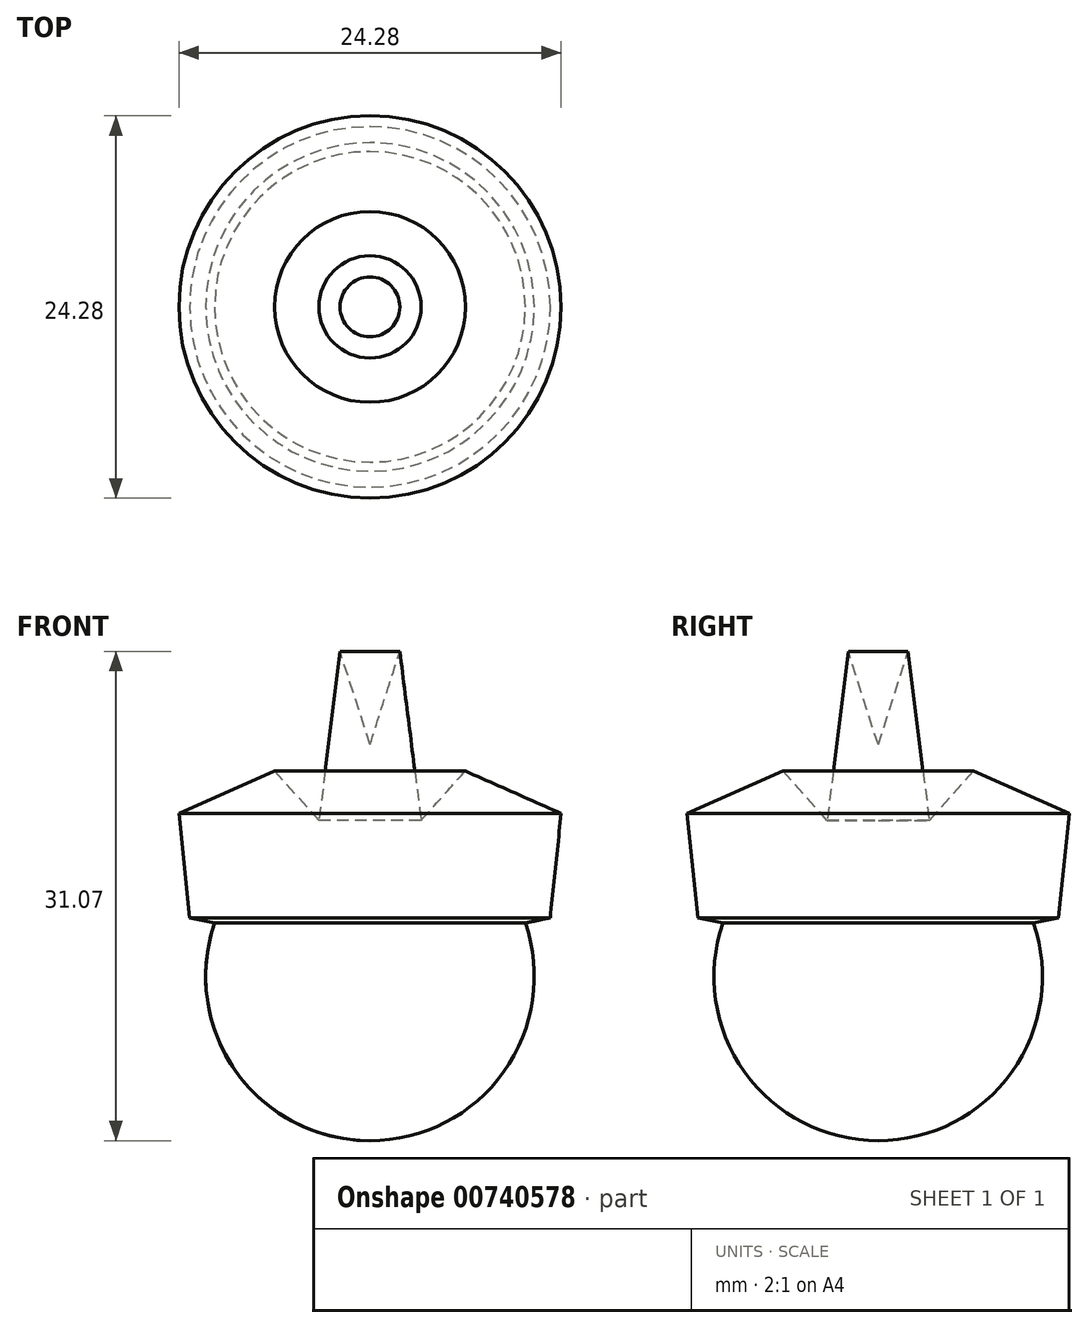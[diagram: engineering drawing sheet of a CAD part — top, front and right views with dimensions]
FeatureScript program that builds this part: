
annotation { "Feature Type Name" : "Feature", "Feature Type Description" : "" }
export const myFeature = defineFeature(function(context is Context, id is Id, definition is map)
    precondition{}
    {
        {
            var Q0;
            Q0=qCreatedBy(makeId("Front.planeOp"),FACE);
            var sketch = newSketch(context, id + "F0", { "sketchPlane" : qUnion([Q0])});
            skArc(sketch, "E0", {"start": v(-9.87, 3.4) * mm, "mid": v(-8.5, -6.06) * mm, "end": v(0, -10.43) * mm});
            skArc(sketch, "E1.cCircle", {"start": v(-3.33, 9.9) * mm, "mid": v(-10.42, 10.81) * mm, "end": v(-9.76, 3.7) * mm, "construction": true});
            skLineSegment(sketch, "E1.0", {"start": v(-12.14, 10.35) * mm, "end": v(-6.06, 13.05) * mm});
            skLineSegment(sketch, "E1.1", {"start": v(-6.06, 13.05) * mm, "end": v(-3.24, 9.92) * mm});
            skLineSegment(sketch, "E1.3", {"start": v(-9.87, 3.4) * mm, "end": v(-11.45, 3.73) * mm});
            skLineSegment(sketch, "E1.4", {"start": v(-11.45, 3.73) * mm, "end": v(-12.14, 10.35) * mm});
            skPoint(sketch, "E1.0.midPoint", {"position": v(-9.1, 11.7) * mm});
            skPoint(sketch, "E2.orphan", {"position": v(-4.94, 2.34) * mm});
            skArc(sketch, "E3.trimOffspring", {"start": v(-3.24, 9.92) * mm, "mid": v(-3.29, 9.9) * mm, "end": v(-3.33, 9.9) * mm});
            skLineSegment(sketch, "E4", {"start": v(0, 14.73) * mm, "end": v(-1.9, 20.64) * mm});
            skLineSegment(sketch, "E5", {"start": v(-1.9, 20.64) * mm, "end": v(-3.24, 9.92) * mm});
            skLineSegment(sketch, "E6", {"start": v(0, 14.73) * mm, "end": v(0, -10.43) * mm});
            skPoint(sketch, "E7.orphan", {"position": v(0, -13.93) * mm});
            skSolve(sketch);
        }
        {
            var Q0;
            Q0=makeQuery(id+"F0.imprint","IMPRINT",FACE,{"disambiguationData":[TD([[makeQuery(id+"F0.imprint","IMPRINT",EDGE,{"derivedFrom":sQuery(id+"F0.wireOp",EDGE,"E0")}),1.0]])]});
            var Q1;
            Q1=sQuery(id+"F0.wireOp",EDGE,"E6");
            revolve(context, id + "F1", {"surfaceOperationType" : NewSurfaceOperationType.NEW, "entities" : qUnion([Q0]), "axis" : qUnion([Q1]), "revolveType" : RevolveType.FULL});
        }
    });
